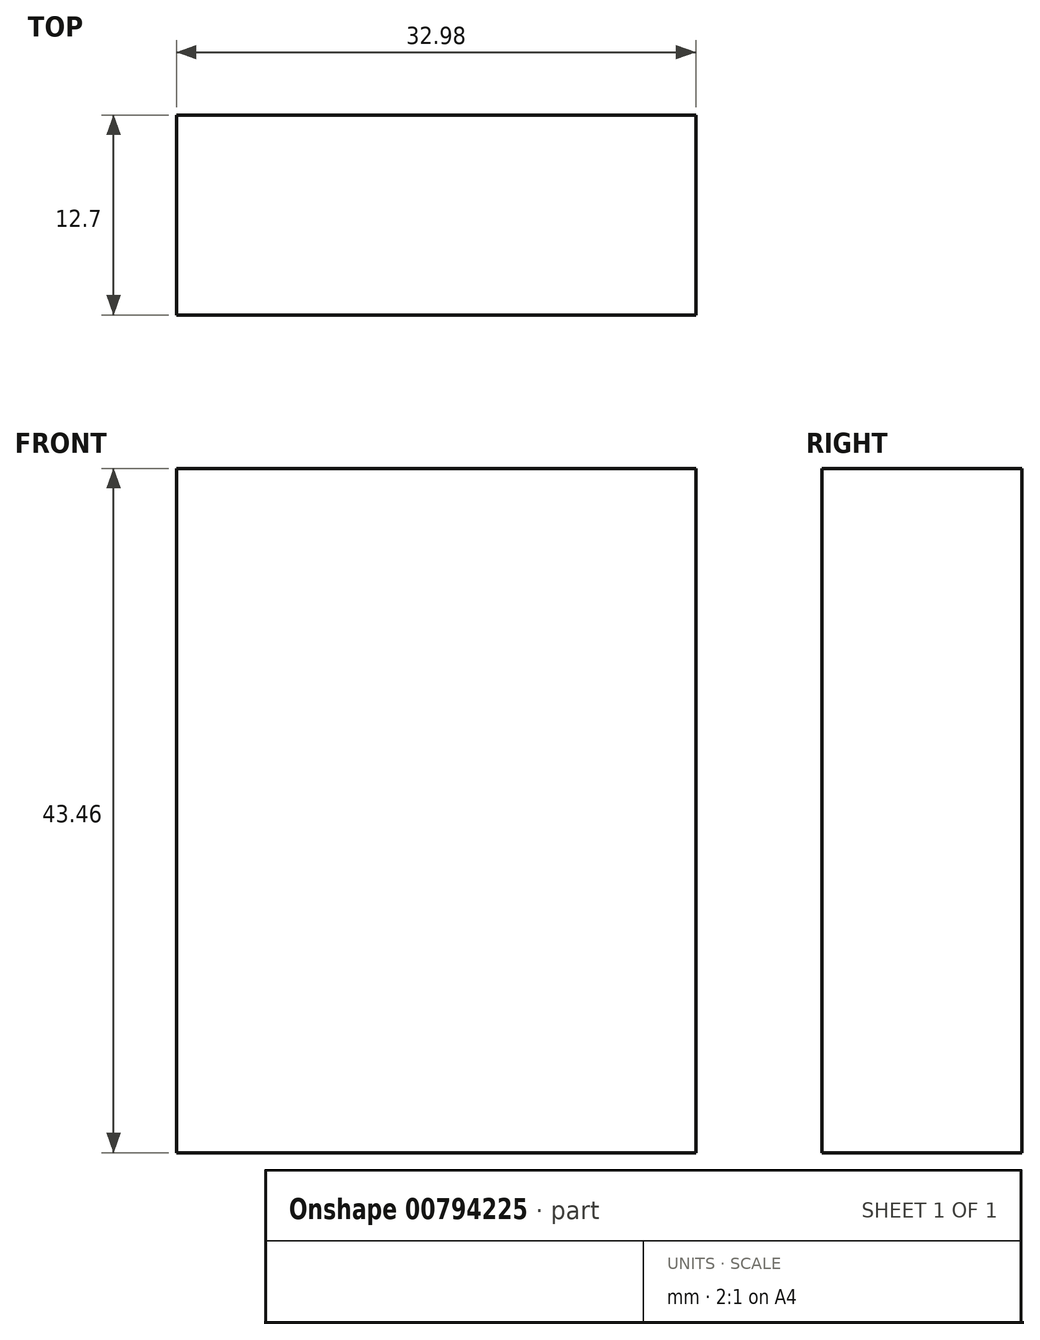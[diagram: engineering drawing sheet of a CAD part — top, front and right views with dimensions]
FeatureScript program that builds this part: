
annotation { "Feature Type Name" : "Feature", "Feature Type Description" : "" }
export const myFeature = defineFeature(function(context is Context, id is Id, definition is map)
    precondition{}
    {
        {
            var Q0;
            Q0=qCreatedBy(makeId("Front.planeOp"),FACE);
            var sketch = newSketch(context, id + "F0", { "sketchPlane" : qUnion([Q0])});
            skLineSegment(sketch, "E0.bottom", {"start": v(-16.49, -21.73) * mm, "end": v(16.49, -21.73) * mm});
            skLineSegment(sketch, "E0.top", {"start": v(-16.49, 21.73) * mm, "end": v(16.49, 21.73) * mm});
            skLineSegment(sketch, "E0.left", {"start": v(-16.49, -21.73) * mm, "end": v(-16.49, 21.73) * mm});
            skLineSegment(sketch, "E0.right", {"start": v(16.49, -21.73) * mm, "end": v(16.49, 21.73) * mm});
            skPoint(sketch, "E0.middle", {"position": v(0, 0) * mm});
            skSolve(sketch);
        }
        {
            var Q0;
            Q0 = qSketchRegion(id + "F0", true);
            extrude(context, id + "F1", {"entities" : qUnion([Q0]), "depth" : 12.7 * mm, "offsetDistance" : 25.4 * mm});
        }
    });
